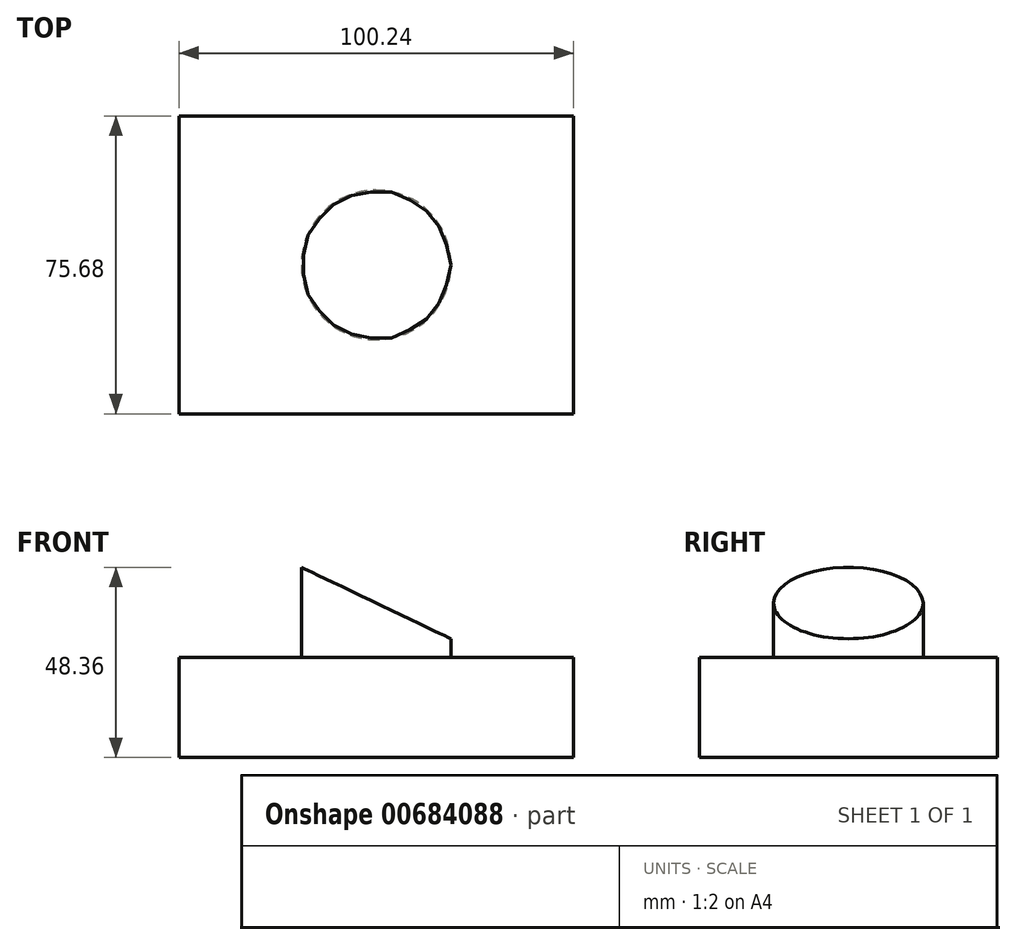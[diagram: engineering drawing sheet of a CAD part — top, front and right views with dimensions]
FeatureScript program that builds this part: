
annotation { "Feature Type Name" : "Feature", "Feature Type Description" : "" }
export const myFeature = defineFeature(function(context is Context, id is Id, definition is map)
    precondition{}
    {
        {
            var Q0;
            Q0=qCreatedBy(makeId("Top.planeOp"),FACE);
            var sketch = newSketch(context, id + "F0", { "sketchPlane" : qUnion([Q0])});
            skLineSegment(sketch, "E0.bottom", {"start": v(-50.12, -37.84) * mm, "end": v(50.12, -37.84) * mm});
            skLineSegment(sketch, "E0.top", {"start": v(-50.12, 37.84) * mm, "end": v(50.12, 37.84) * mm});
            skLineSegment(sketch, "E0.left", {"start": v(-50.12, -37.84) * mm, "end": v(-50.12, 37.84) * mm});
            skLineSegment(sketch, "E0.right", {"start": v(50.12, -37.84) * mm, "end": v(50.12, 37.84) * mm});
            skPoint(sketch, "E0.middle", {"position": v(0, 0) * mm});
            skSolve(sketch);
        }
        {
            var Q0;
            Q0 = qSketchRegion(id + "F0", true);
            extrude(context, id + "F1", {"entities" : qUnion([Q0]), "depth" : 25.4 * mm, "offsetDistance" : 25.4 * mm});
        }
        {
            var Q0;
            Q0=makeQuery(id+"F1.opExtrude","CAP_FACE",FACE,{"disambiguationData":[OSD([sQuery(id+"F0.wireOp",EDGE,"E0.bottom"),sQuery(id+"F0.wireOp",EDGE,"E0.top"),sQuery(id+"F0.wireOp",EDGE,"E0.left"),sQuery(id+"F0.wireOp",EDGE,"E0.right")])],"isStart":false});
            var sketch = newSketch(context, id + "F2", { "sketchPlane" : qUnion([Q0])});
            skCircle(sketch, "E1", {"center": v(0, 0) * mm, "radius": 19.01 * mm});
            skSolve(sketch);
        }
        {
            var Q0;
            Q0 = qSketchRegion(id + "F2", true);
            extrude(context, id + "F3", {"entities" : qUnion([Q0]), "operationType" : NewBodyOperationType.ADD, "depth" : 25.4 * mm, "offsetDistance" : 25.4 * mm});
        }
        {
            var Q0;
            Q0=qCreatedBy(makeId("Front.planeOp"),FACE);
            var sketch = newSketch(context, id + "F4", { "sketchPlane" : qUnion([Q0])});
            skLineSegment(sketch, "E2", {"start": v(-21.61, 49.6) * mm, "end": v(21.3, 29.1) * mm});
            skLineSegment(sketch, "E3", {"start": v(21.3, 29.1) * mm, "end": v(21.3, 59.2) * mm});
            skLineSegment(sketch, "E4", {"start": v(21.3, 59.2) * mm, "end": v(-21.61, 59.2) * mm});
            skLineSegment(sketch, "E5", {"start": v(-21.61, 59.2) * mm, "end": v(-21.61, 49.6) * mm});
            skSolve(sketch);
        }
        {
            var Q0;
            Q0 = qSketchRegion(id + "F4", true);
            extrude(context, id + "F5", {"entities" : qUnion([Q0]), "operationType" : NewBodyOperationType.REMOVE, "endBound" : BoundingType.THROUGH_ALL, "oppositeDirection" : true, "depth" : 25.4 * mm, "offsetDistance" : 25.4 * mm, "hasSecondDirection" : true, "secondDirectionBound" : SecondDirectionBoundingType.THROUGH_ALL, "secondDirectionOppositeDirection" : false, "secondDirectionDepth" : 25.4 * mm});
        }
    });
